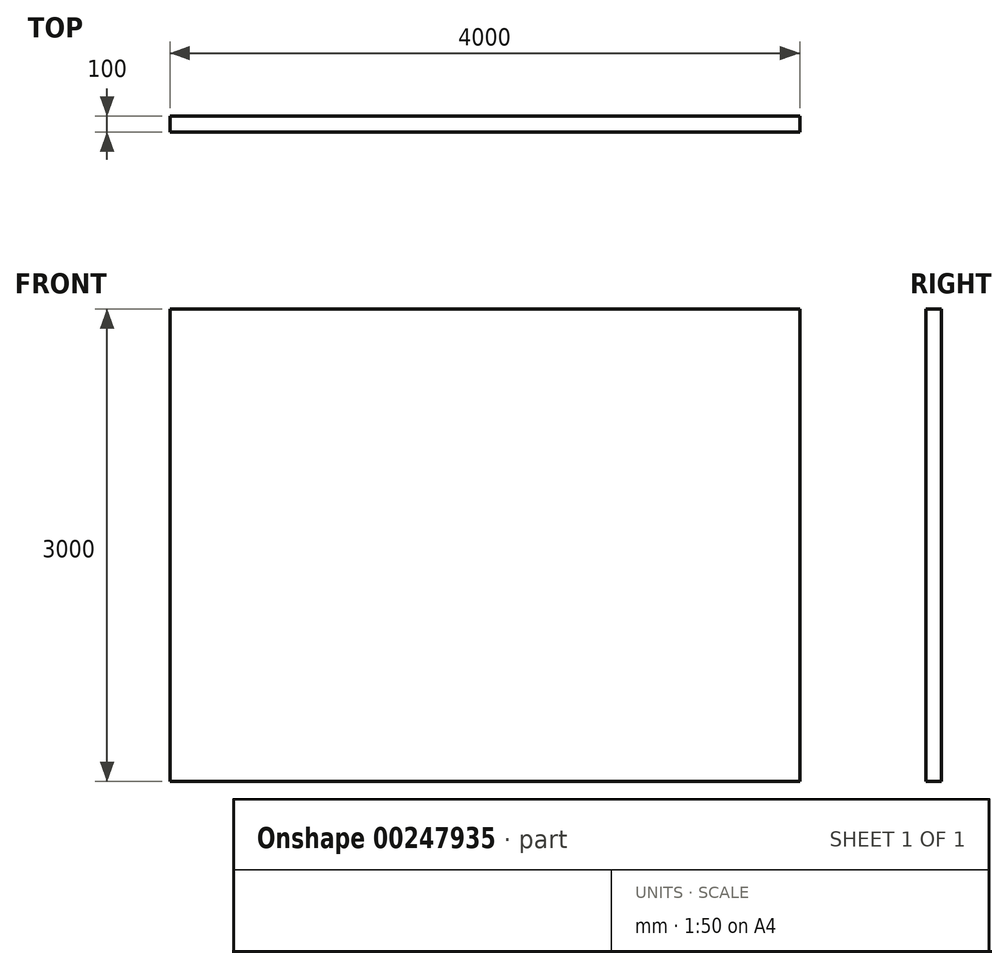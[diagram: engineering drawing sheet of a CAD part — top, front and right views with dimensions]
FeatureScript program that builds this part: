
annotation { "Feature Type Name" : "Feature", "Feature Type Description" : "" }
export const myFeature = defineFeature(function(context is Context, id is Id, definition is map)
    precondition{}
    {
        {
            var Q0;
            Q0=qCreatedBy(makeId("Front.planeOp"),FACE);
            var sketch = newSketch(context, id + "F0", { "sketchPlane" : qUnion([Q0])});
            skLineSegment(sketch, "E0.bottom", {"start": v(2000, 0) * mm, "end": v(-2000, 0) * mm});
            skLineSegment(sketch, "E0.top", {"start": v(2000, 3000) * mm, "end": v(-2000, 3000) * mm});
            skLineSegment(sketch, "E0.left", {"start": v(2000, 0) * mm, "end": v(2000, 3000) * mm});
            skLineSegment(sketch, "E0.right", {"start": v(-2000, 0) * mm, "end": v(-2000, 3000) * mm});
            skPoint(sketch, "E0.middle", {"position": v(0, 1500) * mm});
            skSolve(sketch);
        }
        {
            var Q0;
            Q0=makeQuery(id+"F0.imprint","IMPRINT",FACE,{"disambiguationData":[TD([[makeQuery(id+"F0.imprint","IMPRINT",EDGE,{"derivedFrom":sQuery(id+"F0.wireOp",EDGE,"E0.bottom")}),-1.0]])]});
            extrude(context, id + "F1", {"entities" : qUnion([Q0]), "endBound" : BoundingType.SYMMETRIC, "depth" : 100 * mm});
        }
    });
